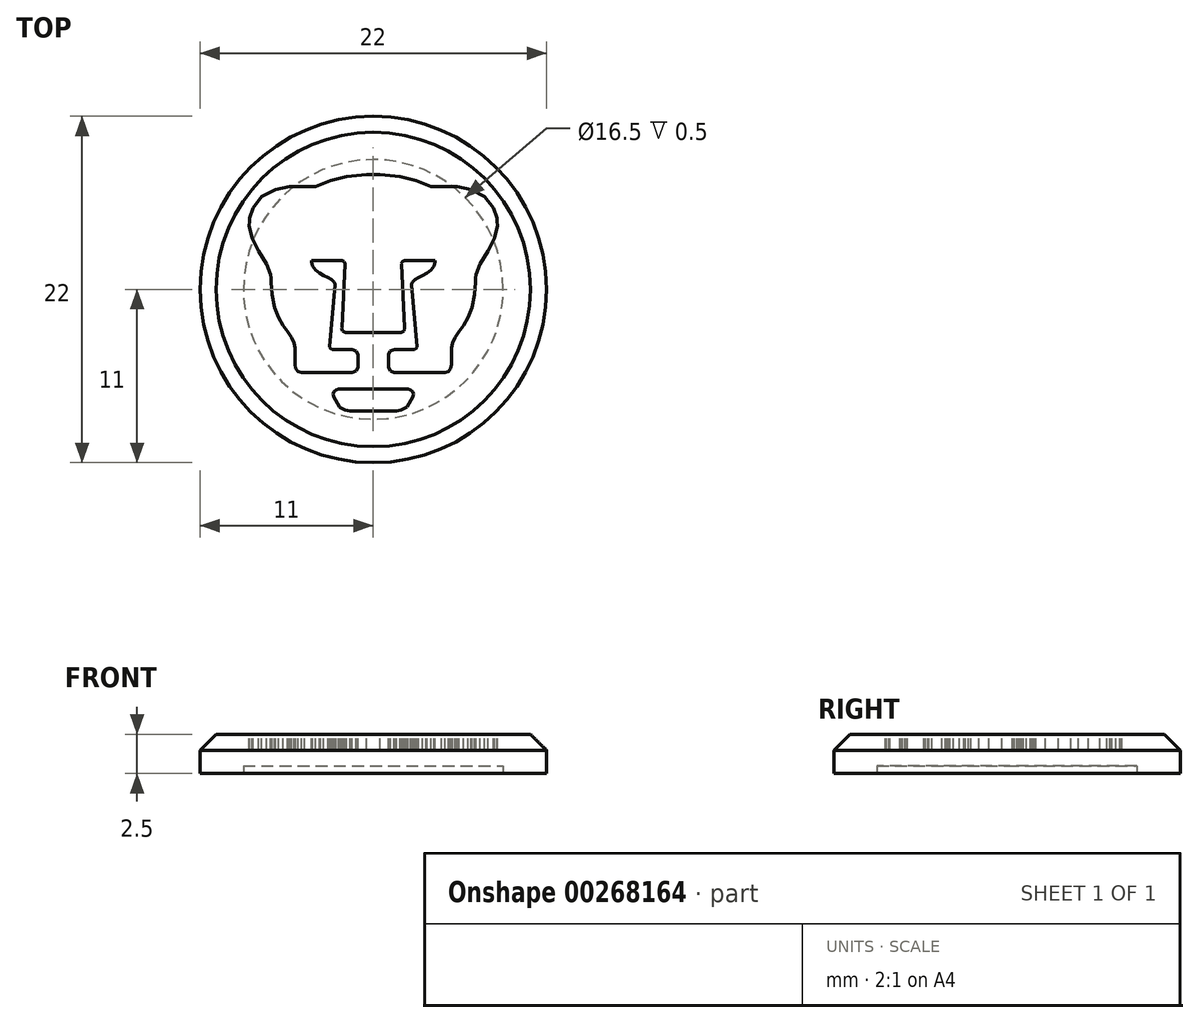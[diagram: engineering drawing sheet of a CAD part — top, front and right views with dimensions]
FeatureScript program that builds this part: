
annotation { "Feature Type Name" : "Feature", "Feature Type Description" : "" }
export const myFeature = defineFeature(function(context is Context, id is Id, definition is map)
    precondition{}
    {
        {
            var Q0;
            Q0=qCreatedBy(makeId("Top.planeOp"),FACE);
            var sketch = newSketch(context, id + "F0", { "sketchPlane" : qUnion([Q0])});
            skCircle(sketch, "E0", {"center": v(0, 0) * mm, "radius": 11 * mm});
            skSolve(sketch);
        }
        {
            var Q0;
            Q0 = qSketchRegion(id + "F0", true);
            extrude(context, id + "F1", {"entities" : qUnion([Q0]), "depth" : 2.5 * mm});
        }
        {
            var Q0;
            Q0=makeQuery(id+"F1.opExtrude","CAP_FACE",FACE,{"disambiguationData":[OSD([sQuery(id+"F0.wireOp",EDGE,"E0")])],"isStart":false});
            var sketch = newSketch(context, id + "F2", { "sketchPlane" : qUnion([Q0])});
            skLineSegment(sketch, "E1", {"start": v(8.41, -15.12) * mm, "end": v(8.87, -15.12) * mm});
            skLineSegment(sketch, "E2", {"start": v(8.87, -15.12) * mm, "end": v(10.24, -14.94) * mm});
            skLineSegment(sketch, "E3", {"start": v(10.24, -14.94) * mm, "end": v(11.95, -14.4) * mm});
            skLineSegment(sketch, "E4", {"start": v(11.95, -14.4) * mm, "end": v(13.5, -13.56) * mm});
            skLineSegment(sketch, "E5", {"start": v(13.5, -13.56) * mm, "end": v(14.84, -12.45) * mm});
            skLineSegment(sketch, "E6", {"start": v(14.84, -12.45) * mm, "end": v(15.95, -11.1) * mm});
            skLineSegment(sketch, "E7", {"start": v(15.95, -11.1) * mm, "end": v(16.79, -9.56) * mm});
            skLineSegment(sketch, "E8", {"start": v(16.79, -9.56) * mm, "end": v(17.32, -7.86) * mm});
            skLineSegment(sketch, "E9", {"start": v(17.32, -7.86) * mm, "end": v(17.5, -6.49) * mm});
            skLineSegment(sketch, "E10", {"start": v(17.5, -6.49) * mm, "end": v(17.5, -6.03) * mm});
            skLineSegment(sketch, "E11", {"start": v(17.5, -6.03) * mm, "end": v(17.5, -5.47) * mm});
            skLineSegment(sketch, "E12", {"start": v(17.5, -5.47) * mm, "end": v(17.22, -3.8) * mm});
            skLineSegment(sketch, "E13", {"start": v(17.22, -3.8) * mm, "end": v(16.58, -2.04) * mm});
            skLineSegment(sketch, "E14", {"start": v(16.58, -2.04) * mm, "end": v(16.4, -1.7) * mm});
            skLineSegment(sketch, "E15", {"start": v(16.4, -1.7) * mm, "end": v(7.99, 12.4) * mm});
            skLineSegment(sketch, "E16", {"start": v(7.99, 12.4) * mm, "end": v(7.84, 12.65) * mm});
            skLineSegment(sketch, "E17", {"start": v(7.84, 12.65) * mm, "end": v(7.34, 13.4) * mm});
            skLineSegment(sketch, "E18", {"start": v(7.34, 13.4) * mm, "end": v(6.57, 14.33) * mm});
            skLineSegment(sketch, "E19", {"start": v(6.57, 14.33) * mm, "end": v(5.69, 15.14) * mm});
            skLineSegment(sketch, "E20", {"start": v(5.69, 15.14) * mm, "end": v(4.7, 15.84) * mm});
            skLineSegment(sketch, "E21", {"start": v(4.7, 15.84) * mm, "end": v(3.63, 16.4) * mm});
            skLineSegment(sketch, "E22", {"start": v(3.63, 16.4) * mm, "end": v(2.48, 16.8) * mm});
            skLineSegment(sketch, "E23", {"start": v(2.48, 16.8) * mm, "end": v(1.27, 17.07) * mm});
            skLineSegment(sketch, "E24", {"start": v(1.27, 17.07) * mm, "end": v(0.32, 17.15) * mm});
            skLineSegment(sketch, "E25", {"start": v(0.32, 17.15) * mm, "end": v(0, 17.15) * mm});
            skLineSegment(sketch, "E26", {"start": v(0, 17.15) * mm, "end": v(-0.32, 17.15) * mm});
            skLineSegment(sketch, "E27", {"start": v(-0.32, 17.15) * mm, "end": v(-1.27, 17.07) * mm});
            skLineSegment(sketch, "E28", {"start": v(-1.27, 17.07) * mm, "end": v(-2.48, 16.8) * mm});
            skLineSegment(sketch, "E29", {"start": v(-2.48, 16.8) * mm, "end": v(-3.63, 16.4) * mm});
            skLineSegment(sketch, "E30", {"start": v(-3.63, 16.4) * mm, "end": v(-4.7, 15.84) * mm});
            skLineSegment(sketch, "E31", {"start": v(-4.7, 15.84) * mm, "end": v(-5.69, 15.14) * mm});
            skLineSegment(sketch, "E32", {"start": v(-5.69, 15.14) * mm, "end": v(-6.57, 14.33) * mm});
            skLineSegment(sketch, "E33", {"start": v(-6.57, 14.33) * mm, "end": v(-7.34, 13.4) * mm});
            skLineSegment(sketch, "E34", {"start": v(-7.34, 13.4) * mm, "end": v(-7.85, 12.65) * mm});
            skLineSegment(sketch, "E35", {"start": v(-7.85, 12.65) * mm, "end": v(-7.99, 12.4) * mm});
            skLineSegment(sketch, "E36", {"start": v(-7.99, 12.4) * mm, "end": v(-16.4, -1.7) * mm});
            skLineSegment(sketch, "E37", {"start": v(-16.4, -1.7) * mm, "end": v(-16.58, -2.04) * mm});
            skLineSegment(sketch, "E38", {"start": v(-16.58, -2.04) * mm, "end": v(-17.22, -3.8) * mm});
            skLineSegment(sketch, "E39", {"start": v(-17.22, -3.8) * mm, "end": v(-17.5, -5.47) * mm});
            skLineSegment(sketch, "E40", {"start": v(-17.5, -5.47) * mm, "end": v(-17.5, -6.03) * mm});
            skLineSegment(sketch, "E41", {"start": v(-17.5, -6.03) * mm, "end": v(-17.5, -6.49) * mm});
            skLineSegment(sketch, "E42", {"start": v(-17.5, -6.49) * mm, "end": v(-17.32, -7.86) * mm});
            skLineSegment(sketch, "E43", {"start": v(-17.32, -7.86) * mm, "end": v(-16.79, -9.56) * mm});
            skLineSegment(sketch, "E44", {"start": v(-16.79, -9.56) * mm, "end": v(-15.95, -11.1) * mm});
            skLineSegment(sketch, "E45", {"start": v(-15.95, -11.1) * mm, "end": v(-14.84, -12.45) * mm});
            skLineSegment(sketch, "E46", {"start": v(-14.84, -12.45) * mm, "end": v(-13.5, -13.56) * mm});
            skLineSegment(sketch, "E47", {"start": v(-13.5, -13.56) * mm, "end": v(-11.95, -14.4) * mm});
            skLineSegment(sketch, "E48", {"start": v(-11.95, -14.4) * mm, "end": v(-10.24, -14.94) * mm});
            skLineSegment(sketch, "E49", {"start": v(-10.24, -14.94) * mm, "end": v(-8.87, -15.12) * mm});
            skLineSegment(sketch, "E50", {"start": v(-8.87, -15.12) * mm, "end": v(-8.41, -15.12) * mm});
            skLineSegment(sketch, "E51", {"start": v(-8.41, -15.12) * mm, "end": v(8.41, -15.12) * mm});
            skLineSegment(sketch, "E52", {"start": v(1.7, -2.74) * mm, "end": v(1.77, -2.73) * mm});
            skLineSegment(sketch, "E53", {"start": v(1.77, -2.73) * mm, "end": v(1.94, -2.63) * mm});
            skLineSegment(sketch, "E54", {"start": v(1.94, -2.63) * mm, "end": v(2, -2.45) * mm});
            skLineSegment(sketch, "E55", {"start": v(2, -2.45) * mm, "end": v(2, -2.4) * mm});
            skLineSegment(sketch, "E56", {"start": v(2, -2.4) * mm, "end": v(1.78, 1.61) * mm});
            skLineSegment(sketch, "E57", {"start": v(1.78, 1.61) * mm, "end": v(1.78, 1.65) * mm});
            skLineSegment(sketch, "E58", {"start": v(1.78, 1.65) * mm, "end": v(1.85, 1.78) * mm});
            skLineSegment(sketch, "E59", {"start": v(1.85, 1.78) * mm, "end": v(2, 1.84) * mm});
            skLineSegment(sketch, "E60", {"start": v(2, 1.84) * mm, "end": v(2.04, 1.84) * mm});
            skLineSegment(sketch, "E61", {"start": v(2.04, 1.84) * mm, "end": v(3.92, 1.84) * mm});
            skLineSegment(sketch, "E62", {"start": v(3.92, 1.84) * mm, "end": v(3.92, 1.75) * mm});
            skLineSegment(sketch, "E63", {"start": v(3.92, 1.75) * mm, "end": v(3.84, 1.49) * mm});
            skLineSegment(sketch, "E64", {"start": v(3.84, 1.49) * mm, "end": v(3.67, 1.23) * mm});
            skLineSegment(sketch, "E65", {"start": v(3.67, 1.23) * mm, "end": v(3.42, 1.03) * mm});
            skLineSegment(sketch, "E66", {"start": v(3.42, 1.03) * mm, "end": v(3.15, 0.88) * mm});
            skLineSegment(sketch, "E67", {"start": v(3.15, 0.88) * mm, "end": v(2.88, 0.76) * mm});
            skLineSegment(sketch, "E68", {"start": v(2.88, 0.76) * mm, "end": v(2.65, 0.63) * mm});
            skLineSegment(sketch, "E69", {"start": v(2.65, 0.63) * mm, "end": v(2.49, 0.48) * mm});
            skLineSegment(sketch, "E70", {"start": v(2.49, 0.48) * mm, "end": v(2.44, 0.34) * mm});
            skLineSegment(sketch, "E71", {"start": v(2.44, 0.34) * mm, "end": v(2.44, 0.3) * mm});
            skLineSegment(sketch, "E72", {"start": v(2.44, 0.3) * mm, "end": v(2.77, -3.63) * mm});
            skLineSegment(sketch, "E73", {"start": v(2.77, -3.63) * mm, "end": v(2.77, -3.66) * mm});
            skLineSegment(sketch, "E74", {"start": v(2.77, -3.66) * mm, "end": v(2.72, -3.76) * mm});
            skLineSegment(sketch, "E75", {"start": v(2.72, -3.76) * mm, "end": v(2.63, -3.81) * mm});
            skLineSegment(sketch, "E76", {"start": v(2.63, -3.81) * mm, "end": v(2.6, -3.81) * mm});
            skLineSegment(sketch, "E77", {"start": v(2.6, -3.81) * mm, "end": v(1.42, -3.81) * mm});
            skLineSegment(sketch, "E78", {"start": v(1.42, -3.81) * mm, "end": v(1.35, -3.81) * mm});
            skLineSegment(sketch, "E79", {"start": v(1.35, -3.81) * mm, "end": v(1.08, -3.92) * mm});
            skLineSegment(sketch, "E80", {"start": v(1.08, -3.92) * mm, "end": v(0.96, -4.15) * mm});
            skLineSegment(sketch, "E81", {"start": v(0.96, -4.15) * mm, "end": v(0.96, -4.22) * mm});
            skLineSegment(sketch, "E82", {"start": v(0.96, -4.22) * mm, "end": v(0.96, -4.87) * mm});
            skLineSegment(sketch, "E83", {"start": v(0.96, -4.87) * mm, "end": v(0.96, -4.95) * mm});
            skLineSegment(sketch, "E84", {"start": v(0.96, -4.95) * mm, "end": v(1.09, -5.18) * mm});
            skLineSegment(sketch, "E85", {"start": v(1.09, -5.18) * mm, "end": v(1.33, -5.28) * mm});
            skLineSegment(sketch, "E86", {"start": v(1.33, -5.28) * mm, "end": v(1.41, -5.28) * mm});
            skLineSegment(sketch, "E87", {"start": v(1.41, -5.28) * mm, "end": v(4.28, -5.28) * mm});
            skLineSegment(sketch, "E88", {"start": v(4.28, -5.28) * mm, "end": v(4.35, -5.28) * mm});
            skLineSegment(sketch, "E89", {"start": v(4.35, -5.28) * mm, "end": v(4.55, -5.27) * mm});
            skLineSegment(sketch, "E90", {"start": v(4.55, -5.27) * mm, "end": v(4.77, -5.2) * mm});
            skLineSegment(sketch, "E91", {"start": v(4.77, -5.2) * mm, "end": v(4.92, -5.02) * mm});
            skLineSegment(sketch, "E92", {"start": v(4.92, -5.02) * mm, "end": v(4.97, -4.76) * mm});
            skLineSegment(sketch, "E93", {"start": v(4.97, -4.76) * mm, "end": v(4.97, -4.68) * mm});
            skLineSegment(sketch, "E94", {"start": v(4.97, -4.68) * mm, "end": v(4.97, -4.46) * mm});
            skLineSegment(sketch, "E95", {"start": v(4.97, -4.46) * mm, "end": v(4.98, -3.88) * mm});
            skLineSegment(sketch, "E96", {"start": v(4.98, -3.88) * mm, "end": v(4.97, -3.8) * mm});
            skLineSegment(sketch, "E97", {"start": v(4.97, -3.8) * mm, "end": v(4.97, -3.7) * mm});
            skLineSegment(sketch, "E98", {"start": v(4.97, -3.7) * mm, "end": v(5.03, -3.4) * mm});
            skLineSegment(sketch, "E99", {"start": v(5.03, -3.4) * mm, "end": v(5.2, -3.04) * mm});
            skLineSegment(sketch, "E100", {"start": v(5.2, -3.04) * mm, "end": v(5.45, -2.68) * mm});
            skLineSegment(sketch, "E101", {"start": v(5.45, -2.68) * mm, "end": v(5.74, -2.28) * mm});
            skLineSegment(sketch, "E102", {"start": v(5.74, -2.28) * mm, "end": v(6.03, -1.78) * mm});
            skLineSegment(sketch, "E103", {"start": v(6.03, -1.78) * mm, "end": v(6.27, -1.15) * mm});
            skLineSegment(sketch, "E104", {"start": v(6.27, -1.15) * mm, "end": v(6.43, -0.33) * mm});
            skLineSegment(sketch, "E105", {"start": v(6.43, -0.33) * mm, "end": v(6.49, 0.46) * mm});
            skLineSegment(sketch, "E106", {"start": v(6.49, 0.46) * mm, "end": v(6.48, 0.72) * mm});
            skLineSegment(sketch, "E107", {"start": v(6.48, 0.72) * mm, "end": v(6.51, 0.96) * mm});
            skLineSegment(sketch, "E108", {"start": v(6.51, 0.96) * mm, "end": v(6.79, 1.63) * mm});
            skLineSegment(sketch, "E109", {"start": v(6.79, 1.63) * mm, "end": v(7.27, 2.43) * mm});
            skLineSegment(sketch, "E110", {"start": v(7.27, 2.43) * mm, "end": v(7.71, 3.27) * mm});
            skLineSegment(sketch, "E111", {"start": v(7.71, 3.27) * mm, "end": v(7.88, 4.06) * mm});
            skLineSegment(sketch, "E112", {"start": v(7.88, 4.06) * mm, "end": v(7.87, 4.31) * mm});
            skLineSegment(sketch, "E113", {"start": v(7.87, 4.31) * mm, "end": v(7.86, 4.53) * mm});
            skLineSegment(sketch, "E114", {"start": v(7.86, 4.53) * mm, "end": v(7.64, 5.19) * mm});
            skLineSegment(sketch, "E115", {"start": v(7.64, 5.19) * mm, "end": v(7.08, 5.89) * mm});
            skLineSegment(sketch, "E116", {"start": v(7.08, 5.89) * mm, "end": v(6.2, 6.36) * mm});
            skLineSegment(sketch, "E117", {"start": v(6.2, 6.36) * mm, "end": v(5.3, 6.53) * mm});
            skLineSegment(sketch, "E118", {"start": v(5.3, 6.53) * mm, "end": v(5.01, 6.53) * mm});
            skLineSegment(sketch, "E119", {"start": v(5.01, 6.53) * mm, "end": v(3.77, 6.53) * mm});
            skLineSegment(sketch, "E120", {"start": v(3.77, 6.53) * mm, "end": v(3.67, 6.53) * mm});
            skLineSegment(sketch, "E121", {"start": v(3.67, 6.53) * mm, "end": v(3.34, 6.65) * mm});
            skLineSegment(sketch, "E122", {"start": v(3.34, 6.65) * mm, "end": v(2.73, 6.9) * mm});
            skLineSegment(sketch, "E123", {"start": v(2.73, 6.9) * mm, "end": v(1.7, 7.17) * mm});
            skLineSegment(sketch, "E124", {"start": v(1.7, 7.17) * mm, "end": v(0.42, 7.28) * mm});
            skLineSegment(sketch, "E125", {"start": v(0.42, 7.28) * mm, "end": v(0, 7.28) * mm});
            skLineSegment(sketch, "E126", {"start": v(0, 7.28) * mm, "end": v(-0.42, 7.28) * mm});
            skLineSegment(sketch, "E127", {"start": v(-0.42, 7.28) * mm, "end": v(-1.7, 7.17) * mm});
            skLineSegment(sketch, "E128", {"start": v(-1.7, 7.17) * mm, "end": v(-2.73, 6.9) * mm});
            skLineSegment(sketch, "E129", {"start": v(-2.73, 6.9) * mm, "end": v(-3.34, 6.65) * mm});
            skLineSegment(sketch, "E130", {"start": v(-3.34, 6.65) * mm, "end": v(-3.67, 6.53) * mm});
            skLineSegment(sketch, "E131", {"start": v(-3.67, 6.53) * mm, "end": v(-3.77, 6.53) * mm});
            skLineSegment(sketch, "E132", {"start": v(-3.77, 6.53) * mm, "end": v(-5.01, 6.53) * mm});
            skLineSegment(sketch, "E133", {"start": v(-5.01, 6.53) * mm, "end": v(-5.3, 6.53) * mm});
            skLineSegment(sketch, "E134", {"start": v(-5.3, 6.53) * mm, "end": v(-6.2, 6.36) * mm});
            skLineSegment(sketch, "E135", {"start": v(-6.2, 6.36) * mm, "end": v(-7.08, 5.89) * mm});
            skLineSegment(sketch, "E136", {"start": v(-7.08, 5.89) * mm, "end": v(-7.65, 5.19) * mm});
            skLineSegment(sketch, "E137", {"start": v(-7.65, 5.19) * mm, "end": v(-7.86, 4.53) * mm});
            skLineSegment(sketch, "E138", {"start": v(-7.86, 4.53) * mm, "end": v(-7.87, 4.31) * mm});
            skLineSegment(sketch, "E139", {"start": v(-7.87, 4.31) * mm, "end": v(-7.88, 4.06) * mm});
            skLineSegment(sketch, "E140", {"start": v(-7.88, 4.06) * mm, "end": v(-7.71, 3.27) * mm});
            skLineSegment(sketch, "E141", {"start": v(-7.71, 3.27) * mm, "end": v(-7.27, 2.43) * mm});
            skLineSegment(sketch, "E142", {"start": v(-7.27, 2.43) * mm, "end": v(-6.79, 1.63) * mm});
            skLineSegment(sketch, "E143", {"start": v(-6.79, 1.63) * mm, "end": v(-6.51, 0.96) * mm});
            skLineSegment(sketch, "E144", {"start": v(-6.51, 0.96) * mm, "end": v(-6.48, 0.72) * mm});
            skLineSegment(sketch, "E145", {"start": v(-6.48, 0.72) * mm, "end": v(-6.49, 0.46) * mm});
            skLineSegment(sketch, "E146", {"start": v(-6.49, 0.46) * mm, "end": v(-6.44, -0.33) * mm});
            skLineSegment(sketch, "E147", {"start": v(-6.44, -0.33) * mm, "end": v(-6.27, -1.15) * mm});
            skLineSegment(sketch, "E148", {"start": v(-6.27, -1.15) * mm, "end": v(-6.03, -1.78) * mm});
            skLineSegment(sketch, "E149", {"start": v(-6.03, -1.78) * mm, "end": v(-5.74, -2.28) * mm});
            skLineSegment(sketch, "E150", {"start": v(-5.74, -2.28) * mm, "end": v(-5.45, -2.68) * mm});
            skLineSegment(sketch, "E151", {"start": v(-5.45, -2.68) * mm, "end": v(-5.2, -3.04) * mm});
            skLineSegment(sketch, "E152", {"start": v(-5.2, -3.04) * mm, "end": v(-5.03, -3.4) * mm});
            skLineSegment(sketch, "E153", {"start": v(-5.03, -3.4) * mm, "end": v(-4.97, -3.7) * mm});
            skLineSegment(sketch, "E154", {"start": v(-4.97, -3.7) * mm, "end": v(-4.98, -3.8) * mm});
            skLineSegment(sketch, "E155", {"start": v(-4.98, -3.8) * mm, "end": v(-4.98, -3.88) * mm});
            skLineSegment(sketch, "E156", {"start": v(-4.98, -3.88) * mm, "end": v(-4.98, -4.48) * mm});
            skLineSegment(sketch, "E157", {"start": v(-4.98, -4.48) * mm, "end": v(-4.98, -4.68) * mm});
            skLineSegment(sketch, "E158", {"start": v(-4.98, -4.68) * mm, "end": v(-4.98, -4.76) * mm});
            skLineSegment(sketch, "E159", {"start": v(-4.98, -4.76) * mm, "end": v(-4.92, -5.02) * mm});
            skLineSegment(sketch, "E160", {"start": v(-4.92, -5.02) * mm, "end": v(-4.77, -5.2) * mm});
            skLineSegment(sketch, "E161", {"start": v(-4.77, -5.2) * mm, "end": v(-4.55, -5.27) * mm});
            skLineSegment(sketch, "E162", {"start": v(-4.55, -5.27) * mm, "end": v(-4.35, -5.28) * mm});
            skLineSegment(sketch, "E163", {"start": v(-4.35, -5.28) * mm, "end": v(-4.28, -5.28) * mm});
            skLineSegment(sketch, "E164", {"start": v(-4.28, -5.28) * mm, "end": v(-1.41, -5.28) * mm});
            skLineSegment(sketch, "E165", {"start": v(-1.41, -5.28) * mm, "end": v(-1.33, -5.28) * mm});
            skLineSegment(sketch, "E166", {"start": v(-1.33, -5.28) * mm, "end": v(-1.09, -5.18) * mm});
            skLineSegment(sketch, "E167", {"start": v(-1.09, -5.18) * mm, "end": v(-0.96, -4.95) * mm});
            skLineSegment(sketch, "E168", {"start": v(-0.96, -4.95) * mm, "end": v(-0.96, -4.87) * mm});
            skLineSegment(sketch, "E169", {"start": v(-0.96, -4.87) * mm, "end": v(-0.96, -4.22) * mm});
            skLineSegment(sketch, "E170", {"start": v(-0.96, -4.22) * mm, "end": v(-0.96, -4.15) * mm});
            skLineSegment(sketch, "E171", {"start": v(-0.96, -4.15) * mm, "end": v(-1.08, -3.92) * mm});
            skLineSegment(sketch, "E172", {"start": v(-1.08, -3.92) * mm, "end": v(-1.35, -3.81) * mm});
            skLineSegment(sketch, "E173", {"start": v(-1.35, -3.81) * mm, "end": v(-1.42, -3.81) * mm});
            skLineSegment(sketch, "E174", {"start": v(-1.42, -3.81) * mm, "end": v(-2.6, -3.81) * mm});
            skLineSegment(sketch, "E175", {"start": v(-2.6, -3.81) * mm, "end": v(-2.63, -3.81) * mm});
            skLineSegment(sketch, "E176", {"start": v(-2.63, -3.81) * mm, "end": v(-2.72, -3.76) * mm});
            skLineSegment(sketch, "E177", {"start": v(-2.72, -3.76) * mm, "end": v(-2.77, -3.66) * mm});
            skLineSegment(sketch, "E178", {"start": v(-2.77, -3.66) * mm, "end": v(-2.77, -3.63) * mm});
            skLineSegment(sketch, "E179", {"start": v(-2.77, -3.63) * mm, "end": v(-2.44, 0.3) * mm});
            skLineSegment(sketch, "E180", {"start": v(-2.44, 0.3) * mm, "end": v(-2.44, 0.34) * mm});
            skLineSegment(sketch, "E181", {"start": v(-2.44, 0.34) * mm, "end": v(-2.49, 0.48) * mm});
            skLineSegment(sketch, "E182", {"start": v(-2.49, 0.48) * mm, "end": v(-2.64, 0.63) * mm});
            skLineSegment(sketch, "E183", {"start": v(-2.64, 0.63) * mm, "end": v(-2.88, 0.76) * mm});
            skLineSegment(sketch, "E184", {"start": v(-2.88, 0.76) * mm, "end": v(-3.15, 0.88) * mm});
            skLineSegment(sketch, "E185", {"start": v(-3.15, 0.88) * mm, "end": v(-3.42, 1.03) * mm});
            skLineSegment(sketch, "E186", {"start": v(-3.42, 1.03) * mm, "end": v(-3.67, 1.23) * mm});
            skLineSegment(sketch, "E187", {"start": v(-3.67, 1.23) * mm, "end": v(-3.84, 1.49) * mm});
            skLineSegment(sketch, "E188", {"start": v(-3.84, 1.49) * mm, "end": v(-3.92, 1.75) * mm});
            skLineSegment(sketch, "E189", {"start": v(-3.92, 1.75) * mm, "end": v(-3.92, 1.84) * mm});
            skLineSegment(sketch, "E190", {"start": v(-3.92, 1.84) * mm, "end": v(-2.04, 1.84) * mm});
            skLineSegment(sketch, "E191", {"start": v(-2.04, 1.84) * mm, "end": v(-2, 1.84) * mm});
            skLineSegment(sketch, "E192", {"start": v(-2, 1.84) * mm, "end": v(-1.85, 1.78) * mm});
            skLineSegment(sketch, "E193", {"start": v(-1.85, 1.78) * mm, "end": v(-1.78, 1.65) * mm});
            skLineSegment(sketch, "E194", {"start": v(-1.78, 1.65) * mm, "end": v(-1.78, 1.61) * mm});
            skLineSegment(sketch, "E195", {"start": v(-1.78, 1.61) * mm, "end": v(-2, -2.4) * mm});
            skLineSegment(sketch, "E196", {"start": v(-2, -2.4) * mm, "end": v(-2, -2.45) * mm});
            skLineSegment(sketch, "E197", {"start": v(-2, -2.45) * mm, "end": v(-1.94, -2.63) * mm});
            skLineSegment(sketch, "E198", {"start": v(-1.94, -2.63) * mm, "end": v(-1.77, -2.73) * mm});
            skLineSegment(sketch, "E199", {"start": v(-1.77, -2.73) * mm, "end": v(-1.7, -2.74) * mm});
            skLineSegment(sketch, "E200", {"start": v(-1.7, -2.74) * mm, "end": v(1.7, -2.74) * mm});
            skLineSegment(sketch, "E201", {"start": v(1.36, -7.72) * mm, "end": v(1.46, -7.72) * mm});
            skLineSegment(sketch, "E202", {"start": v(1.46, -7.72) * mm, "end": v(1.78, -7.66) * mm});
            skLineSegment(sketch, "E203", {"start": v(1.78, -7.66) * mm, "end": v(2.1, -7.5) * mm});
            skLineSegment(sketch, "E204", {"start": v(2.1, -7.5) * mm, "end": v(2.14, -7.45) * mm});
            skLineSegment(sketch, "E205", {"start": v(2.14, -7.45) * mm, "end": v(2.51, -6.8) * mm});
            skLineSegment(sketch, "E206", {"start": v(2.51, -6.8) * mm, "end": v(2.53, -6.76) * mm});
            skLineSegment(sketch, "E207", {"start": v(2.53, -6.76) * mm, "end": v(2.55, -6.64) * mm});
            skLineSegment(sketch, "E208", {"start": v(2.55, -6.64) * mm, "end": v(2.5, -6.49) * mm});
            skLineSegment(sketch, "E209", {"start": v(2.5, -6.49) * mm, "end": v(2.36, -6.38) * mm});
            skLineSegment(sketch, "E210", {"start": v(2.36, -6.38) * mm, "end": v(2.2, -6.34) * mm});
            skLineSegment(sketch, "E211", {"start": v(2.2, -6.34) * mm, "end": v(2.14, -6.34) * mm});
            skLineSegment(sketch, "E212", {"start": v(2.14, -6.34) * mm, "end": v(-2.14, -6.34) * mm});
            skLineSegment(sketch, "E213", {"start": v(-2.14, -6.34) * mm, "end": v(-2.2, -6.34) * mm});
            skLineSegment(sketch, "E214", {"start": v(-2.2, -6.34) * mm, "end": v(-2.36, -6.38) * mm});
            skLineSegment(sketch, "E215", {"start": v(-2.36, -6.38) * mm, "end": v(-2.5, -6.49) * mm});
            skLineSegment(sketch, "E216", {"start": v(-2.5, -6.49) * mm, "end": v(-2.55, -6.64) * mm});
            skLineSegment(sketch, "E217", {"start": v(-2.55, -6.64) * mm, "end": v(-2.53, -6.76) * mm});
            skLineSegment(sketch, "E218", {"start": v(-2.53, -6.76) * mm, "end": v(-2.51, -6.8) * mm});
            skLineSegment(sketch, "E219", {"start": v(-2.51, -6.8) * mm, "end": v(-2.14, -7.45) * mm});
            skLineSegment(sketch, "E220", {"start": v(-2.14, -7.45) * mm, "end": v(-2.1, -7.5) * mm});
            skLineSegment(sketch, "E221", {"start": v(-2.1, -7.5) * mm, "end": v(-1.78, -7.66) * mm});
            skLineSegment(sketch, "E222", {"start": v(-1.78, -7.66) * mm, "end": v(-1.46, -7.72) * mm});
            skLineSegment(sketch, "E223", {"start": v(-1.46, -7.72) * mm, "end": v(-1.36, -7.72) * mm});
            skLineSegment(sketch, "E224", {"start": v(-1.36, -7.72) * mm, "end": v(1.36, -7.72) * mm});
            skSolve(sketch);
        }
        {
            var Q0;
            Q0=makeQuery(id+"F2.imprint","IMPRINT",FACE,{"disambiguationData":[TD([[makeQuery(id+"F2.imprint","IMPRINT",EDGE,{"derivedFrom":sQuery(id+"F2.wireOp",EDGE,"E52")}),1.0]])]});
            var Q1;
            Q1=makeQuery(id+"F2.imprint","IMPRINT",FACE,{"disambiguationData":[TD([[makeQuery(id+"F2.imprint","IMPRINT",EDGE,{"derivedFrom":sQuery(id+"F2.wireOp",EDGE,"E201")}),1.0]])]});
            extrude(context, id + "F3", {"entities" : qUnion([Q0, Q1]), "operationType" : NewBodyOperationType.REMOVE, "oppositeDirection" : true, "depth" : 1 * mm});
        }
        {
            var Q0;
            Q0=makeQuery(id+"F1.opExtrude","CAP_EDGE",EDGE,{"disambiguationData":[OSD([sQuery(id+"F0.wireOp",EDGE,"E0")])],"isStart":false});
            chamfer(context, id + "F4", {"entities" : qUnion([Q0]), "width" : 1.02 * mm, "tangentPropagation" : true});
        }
        {
            var Q0;
            Q0=makeQuery(id+"F1.opExtrude","CAP_FACE",FACE,{"disambiguationData":[OSD([sQuery(id+"F0.wireOp",EDGE,"E0")])],"isStart":true});
            var sketch = newSketch(context, id + "F5", { "sketchPlane" : qUnion([Q0])});
            skCircle(sketch, "E225", {"center": v(0, 0) * mm, "radius": 8.25 * mm});
            skSolve(sketch);
        }
        {
            var Q0;
            Q0 = qSketchRegion(id + "F5", true);
            extrude(context, id + "F6", {"entities" : qUnion([Q0]), "operationType" : NewBodyOperationType.REMOVE, "oppositeDirection" : true, "depth" : .5 * mm});
        }
    });
